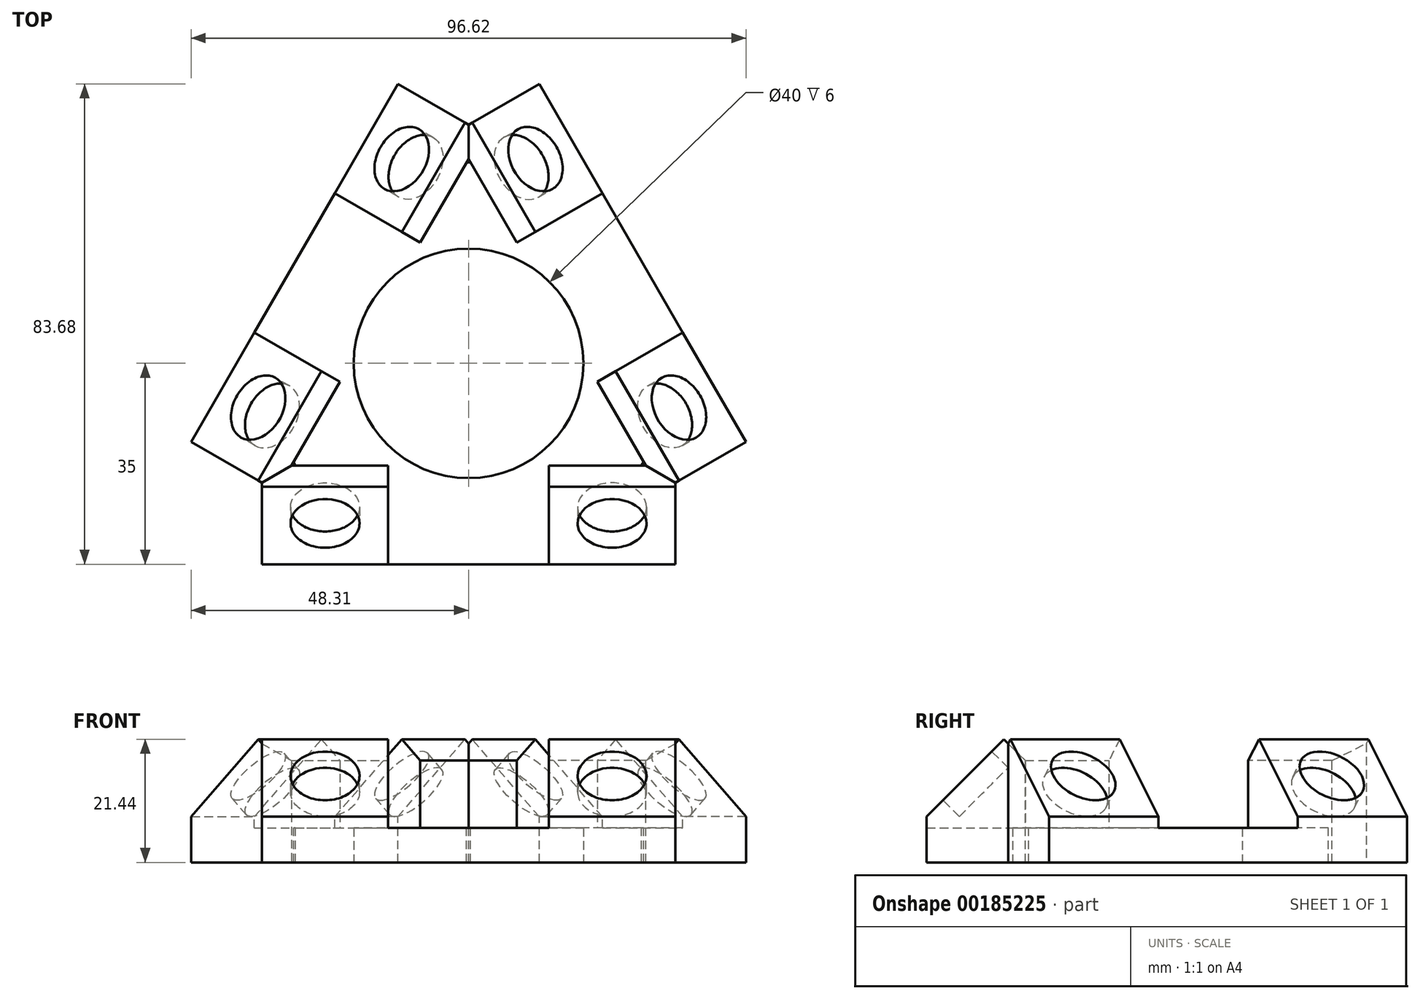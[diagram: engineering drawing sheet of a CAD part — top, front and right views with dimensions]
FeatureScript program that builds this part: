
annotation { "Feature Type Name" : "Feature", "Feature Type Description" : "" }
export const myFeature = defineFeature(function(context is Context, id is Id, definition is map)
    precondition{}
    {
        {
            var Q0;
            Q0=qCreatedBy(makeId("Top.planeOp"),FACE);
            var sketch = newSketch(context, id + "F0", { "sketchPlane" : qUnion([Q0])});
            skCircle(sketch, "E0.cCircle", {"center": v(0, 0) * mm, "radius": 35 * mm, "construction": true});
            skLineSegment(sketch, "E0.0", {"start": v(-20.2, 35) * mm, "end": v(20.2, 35) * mm});
            skLineSegment(sketch, "E0.1", {"start": v(20.2, 35) * mm, "end": v(40.41, 0) * mm});
            skLineSegment(sketch, "E0.2", {"start": v(40.41, 0) * mm, "end": v(20.2, -35) * mm});
            skLineSegment(sketch, "E0.3", {"start": v(20.2, -35) * mm, "end": v(-20.2, -35) * mm});
            skLineSegment(sketch, "E0.4", {"start": v(-20.2, -35) * mm, "end": v(-40.41, 0) * mm});
            skLineSegment(sketch, "E0.5", {"start": v(-40.41, 0) * mm, "end": v(-20.2, 35) * mm});
            skPoint(sketch, "E0.0.midPoint", {"position": v(0, 35) * mm});
            skCircle(sketch, "E1", {"center": v(0, 0) * mm, "radius": 20 * mm});
            skCircle(sketch, "E2", {"center": v(9.15, 34.15) * mm, "radius": 6 * mm, "construction": true});
            skCircle(sketch, "E3.MirrorC", {"center": v(-9.15, 34.15) * mm, "radius": 6 * mm, "construction": true});
            skLineSegment(sketch, "E4", {"start": v(0, 0) * mm, "end": v(30.31, 17.5) * mm, "construction": true});
            skCircle(sketch, "E5.MirrorC", {"center": v(34.15, -9.15) * mm, "radius": 6 * mm, "construction": true});
            skCircle(sketch, "E6.MirrorC", {"center": v(25, -25) * mm, "radius": 6 * mm, "construction": true});
            skCircle(sketch, "E7.MirrorC", {"center": v(-34.15, -9.15) * mm, "radius": 6 * mm, "construction": true});
            skCircle(sketch, "E8.MirrorC", {"center": v(-25, -25) * mm, "radius": 6 * mm, "construction": true});
            skLineSegment(sketch, "E9", {"start": v(9.15, 34.15) * mm, "end": v(34.15, -9.15) * mm, "construction": true});
            skSolve(sketch);
        }
        {
            var Q0;
            Q0=makeQuery(id+"F0.imprint","IMPRINT",FACE,{"disambiguationData":[TD([[makeQuery(id+"F0.imprint","IMPRINT",EDGE,{"derivedFrom":sQuery(id+"F0.wireOp",EDGE,"E0.0")}),-1.0]])]});
            extrude(context, id + "F1", {"entities" : qUnion([Q0]), "depth" : 6 * mm});
        }
        {
            var Q0;
            Q0=qCreatedBy(makeId("Right.planeOp"),FACE);
            var sketch = newSketch(context, id + "F2", { "sketchPlane" : qUnion([Q0])});
            skLineSegment(sketch, "E10", {"start": v(-32.12, 10.83) * mm, "end": v(-29.3, 8) * mm});
            skLineSegment(sketch, "E11", {"start": v(-29.3, 8) * mm, "end": v(-20.8, 16.49) * mm});
            skLineSegment(sketch, "E12", {"start": v(-20.8, 16.49) * mm, "end": v(-23.64, 19.31) * mm});
            skLineSegment(sketch, "E13", {"start": v(-23.64, 19.31) * mm, "end": v(-32.12, 10.83) * mm});
            skLineSegment(sketch, "E14", {"start": v(-25.05, 12.24) * mm, "end": v(-30, 17.2) * mm, "construction": true});
            skLineSegment(sketch, "E15", {"start": v(-23.64, 19.31) * mm, "end": v(-21.51, 21.44) * mm});
            skLineSegment(sketch, "E16", {"start": v(-21.51, 21.44) * mm, "end": v(-17.8, 17.73) * mm});
            skLineSegment(sketch, "E17", {"start": v(-17.8, 17.73) * mm, "end": v(-17.8, 0) * mm});
            skLineSegment(sketch, "E18", {"start": v(-17.8, 0) * mm, "end": v(-35, 0) * mm});
            skLineSegment(sketch, "E19", {"start": v(-35, 0) * mm, "end": v(-35, 7.95) * mm});
            skLineSegment(sketch, "E20", {"start": v(-35, 7.95) * mm, "end": v(-32.12, 10.83) * mm});
            skLineSegment(sketch, "E21.0", {"start": v(0, 6) * mm, "end": v(-35, 6) * mm, "construction": true});
            skSolve(sketch);
        }
        {
            var Q0;
            Q0=makeQuery(id+"F2.imprint","IMPRINT",FACE,{"disambiguationData":[TD([[makeQuery(id+"F2.imprint","IMPRINT",EDGE,{"derivedFrom":sQuery(id+"F2.wireOp",EDGE,"E10")}),-1.0]])]});
            var Q1;
            Q1=makeQuery(id+"F2.imprint","IMPRINT",FACE,{"disambiguationData":[TD([[makeQuery(id+"F2.imprint","IMPRINT",EDGE,{"derivedFrom":sQuery(id+"F2.wireOp",EDGE,"E10")}),1.0]])]});
            extrude(context, id + "F3", {"entities" : qUnion([Q0, Q1]), "operationType" : NewBodyOperationType.ADD, "depth" : 36 * mm, "hasSecondDirection" : true, "secondDirectionOppositeDirection" : false, "secondDirectionDepth" : (36 - 12 - 10) * mm});
        }
        {
            var Q0;
            Q0=makeQuery(id+"F3.opExtrude","SWEPT_FACE",FACE,{"disambiguationData":[OSD([sQuery(id+"F2.wireOp",EDGE,"E13"),sQuery(id+"F2.wireOp",EDGE,"E15"),sQuery(id+"F2.wireOp",EDGE,"E20")])]});
            var sketch = newSketch(context, id + "F4", { "sketchPlane" : qUnion([Q0])});
            skLineSegment(sketch, "E22.0", {"start": v(36, -0.06) * mm, "end": v(14, -0.06) * mm, "construction": true});
            skLineSegment(sketch, "E23", {"start": v(25, -0.06) * mm, "end": v(25, -9.06) * mm, "construction": true});
            skCircle(sketch, "E24", {"center": v(25, -9.06) * mm, "radius": 6 * mm});
            skSolve(sketch);
        }
        {
            var Q0;
            Q0=makeQuery(id+"F4.imprint","IMPRINT",FACE,{"disambiguationData":[TD([[makeQuery(id+"F4.imprint","IMPRINT",EDGE,{"derivedFrom":sQuery(id+"F4.wireOp",EDGE,"E24")}),1.0]])]});
            extrude(context, id + "F5", {"entities" : qUnion([Q0]), "operationType" : NewBodyOperationType.REMOVE, "oppositeDirection" : true, "depth" : 4 * mm});
        }
        {
            var Q0;
            Q0=makeQuery(id+"F1.opExtrude","SWEPT_BODY",BODY,{"disambiguationData":[OSD([sQuery(id+"F0.wireOp",EDGE,"E0.0"),sQuery(id+"F0.wireOp",EDGE,"E0.1"),sQuery(id+"F0.wireOp",EDGE,"E0.2"),sQuery(id+"F0.wireOp",EDGE,"E0.3"),sQuery(id+"F0.wireOp",EDGE,"E0.4"),sQuery(id+"F0.wireOp",EDGE,"E0.5"),sQuery(id+"F0.wireOp",EDGE,"E1")])]});
            var Q1;
            Q1=qCreatedBy(makeId("Right.planeOp"),FACE);
            mirror(context, id + "F6", {"operationType" : NewBodyOperationType.ADD, "entities" : qUnion([Q0]), "mirrorPlane" : qUnion([Q1])});
        }
        {
            var Q0;
            Q0=makeQuery(id+"F1.opExtrude","SWEPT_BODY",BODY,{"disambiguationData":[OSD([sQuery(id+"F0.wireOp",EDGE,"E0.0"),sQuery(id+"F0.wireOp",EDGE,"E0.1"),sQuery(id+"F0.wireOp",EDGE,"E0.2"),sQuery(id+"F0.wireOp",EDGE,"E0.3"),sQuery(id+"F0.wireOp",EDGE,"E0.4"),sQuery(id+"F0.wireOp",EDGE,"E0.5"),sQuery(id+"F0.wireOp",EDGE,"E1")])]});
            var Q1;
            Q1=makeQuery(id+"F1.opExtrude","SWEPT_FACE",FACE,{"disambiguationData":[OSD([sQuery(id+"F0.wireOp",EDGE,"E1")])]});
            circularPattern(context, id + "F7", {"operationType" : NewBodyOperationType.ADD, "entities" : qUnion([Q0]), "axis" : qUnion([Q1]), "angle" : 360 * degree, "instanceCount" : 3, "equalSpace" : true});
        }
    });
